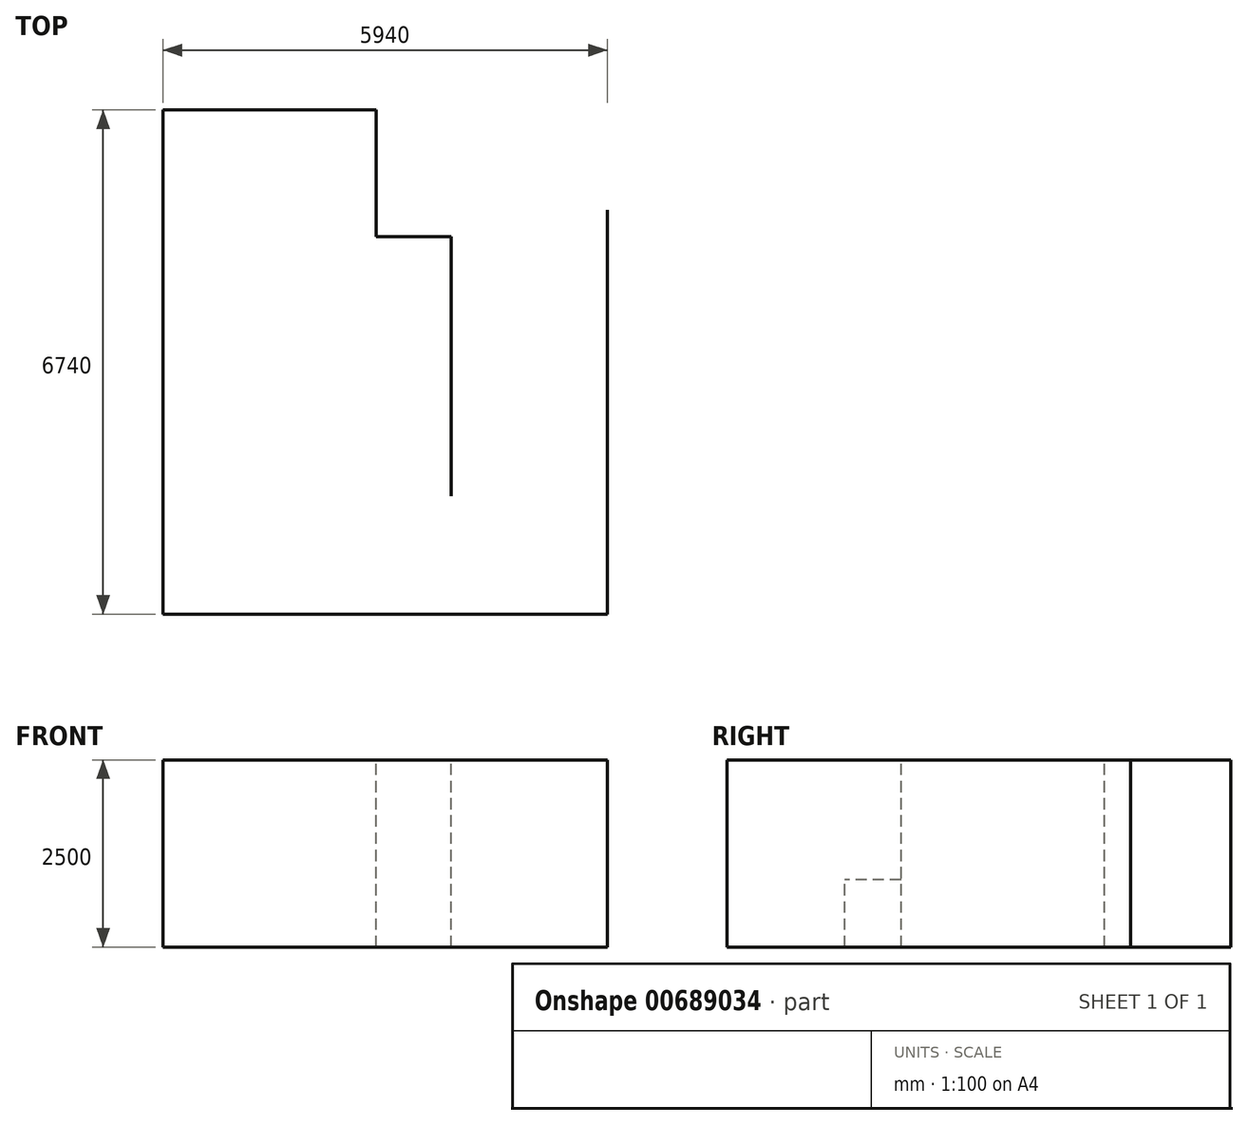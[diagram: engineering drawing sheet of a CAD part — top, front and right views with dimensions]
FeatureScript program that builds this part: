
annotation { "Feature Type Name" : "Feature", "Feature Type Description" : "" }
export const myFeature = defineFeature(function(context is Context, id is Id, definition is map)
    precondition{}
    {
        {
            var Q0;
            Q0=qCreatedBy(makeId("Top.planeOp"),FACE);
            var sketch = newSketch(context, id + "F0", { "sketchPlane" : qUnion([Q0])});
            skLineSegment(sketch, "E0", {"start": v(0, 0) * mm, "end": v(0, 6740) * mm});
            skLineSegment(sketch, "E1", {"start": v(0, 6740) * mm, "end": v(2850, 6740) * mm});
            skLineSegment(sketch, "E2", {"start": v(2850, 6740) * mm, "end": v(2850, 5050) * mm});
            skLineSegment(sketch, "E3", {"start": v(2850, 5050) * mm, "end": v(3850, 5050) * mm});
            skLineSegment(sketch, "E4", {"start": v(3850, 5050) * mm, "end": v(3850, 2330) * mm});
            skLineSegment(sketch, "E5", {"start": v(0, 0) * mm, "end": v(5940, 0) * mm});
            skLineSegment(sketch, "E6", {"start": v(5940, 0) * mm, "end": v(5940, 5402.97) * mm});
            skSolve(sketch);
        }
        {
            var Q0;
            Q0 = qConstructionFilter(qBodyType(qCreatedBy(id + "F0" ,EDGE), BodyType.WIRE), ConstructionObject.NO);
            extrude(context, id + "F1", {"bodyType" : ToolBodyType.SURFACE, "surfaceEntities" : qUnion([Q0]), "depth" : 2500 * mm, "offsetDistance" : 25 * mm});
        }
        {
            var Q0;
            Q0=qCreatedBy(makeId("Top.planeOp"),FACE);
            var sketch = newSketch(context, id + "F2", { "sketchPlane" : qUnion([Q0])});
            skLineSegment(sketch, "E7", {"start": v(3850, 2330) * mm, "end": v(3850, 1580) * mm});
            skSolve(sketch);
        }
        {
            var Q0;
            Q0 = qSketchRegion(id + "F2", true);
            var Q1;
            Q1 = qConstructionFilter(qBodyType(qCreatedBy(id + "F2" ,EDGE), BodyType.WIRE), ConstructionObject.NO);
            extrude(context, id + "F3", {"entities" : qUnion([Q0]), "bodyType" : ToolBodyType.SURFACE, "surfaceEntities" : qUnion([Q1]), "depth" : 900 * mm, "offsetDistance" : 25 * mm});
        }
    });
